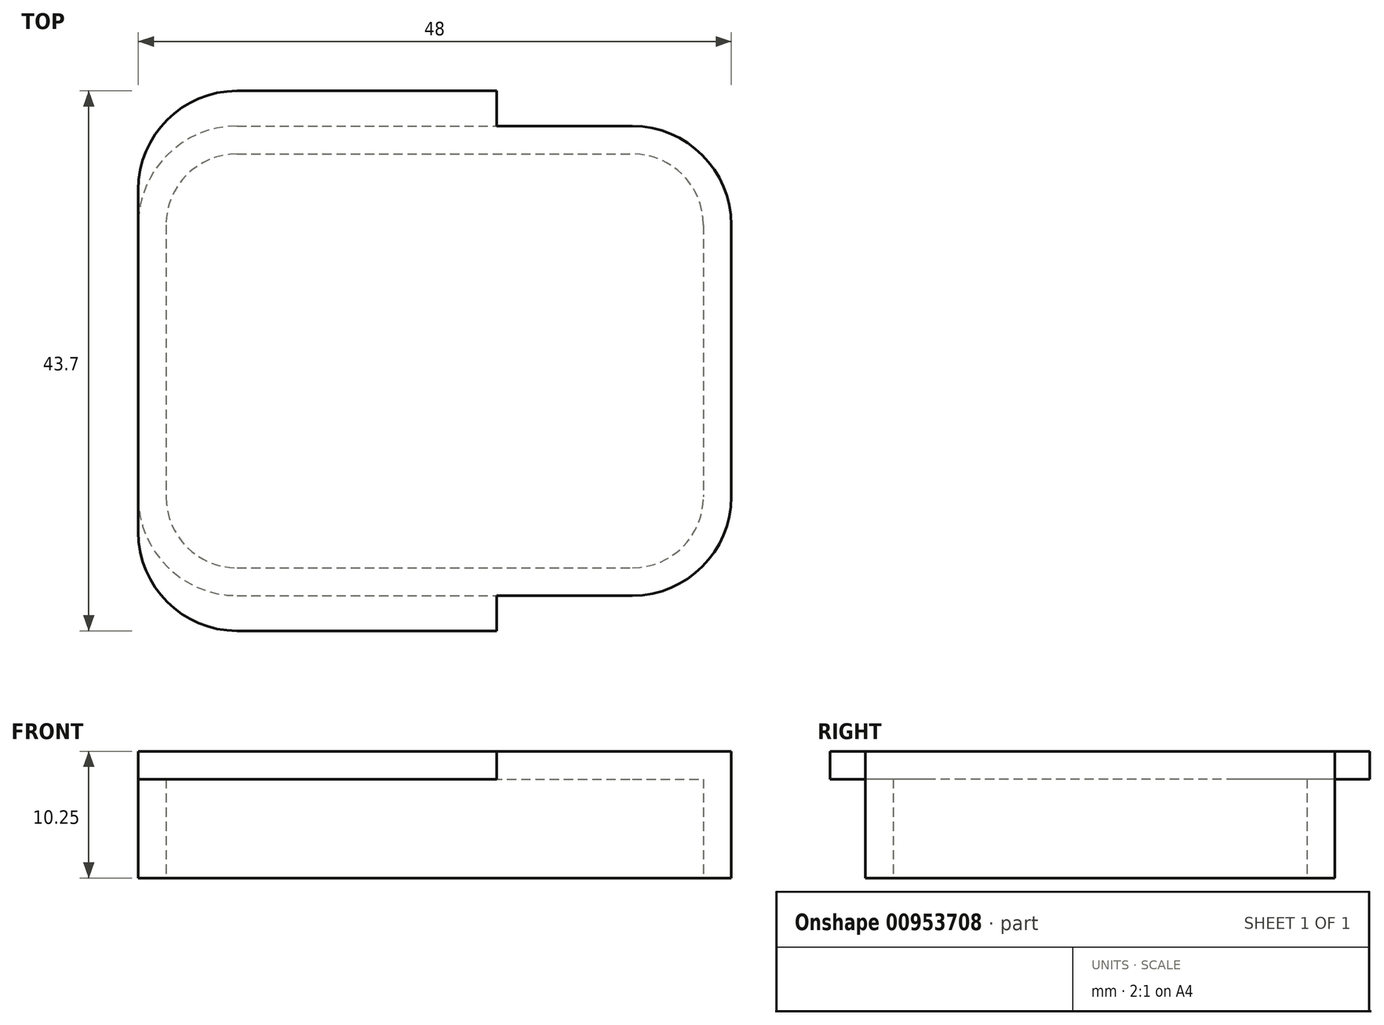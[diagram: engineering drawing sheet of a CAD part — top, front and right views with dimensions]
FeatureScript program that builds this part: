
annotation { "Feature Type Name" : "Feature", "Feature Type Description" : "" }
export const myFeature = defineFeature(function(context is Context, id is Id, definition is map)
    precondition{}
    {
        {
            var Q0;
            Q0=qCreatedBy(makeId("Top.planeOp"),FACE);
            var sketch = newSketch(context, id + "F0", { "sketchPlane" : qUnion([Q0])});
            skLineSegment(sketch, "E0.bottom", {"start": v(-16, 19) * mm, "end": v(16, 19) * mm});
            skLineSegment(sketch, "E0.top", {"start": v(-16, -19) * mm, "end": v(16, -19) * mm});
            skLineSegment(sketch, "E0.left", {"start": v(-24, 11) * mm, "end": v(-24, -11) * mm});
            skLineSegment(sketch, "E0.right", {"start": v(24, 11) * mm, "end": v(24, -11) * mm});
            skPoint(sketch, "E1.visualSharp", {"position": v(24, 19) * mm});
            skArc(sketch, "E1.filletArc", {"start": v(24, 11) * mm, "mid": v(21.66, 16.66) * mm, "end": v(16, 19) * mm});
            skPoint(sketch, "E2.visualSharp", {"position": v(24, -19) * mm});
            skArc(sketch, "E2.filletArc", {"start": v(16, -19) * mm, "mid": v(21.66, -16.66) * mm, "end": v(24, -11) * mm});
            skPoint(sketch, "E3.visualSharp", {"position": v(-24, -19) * mm});
            skArc(sketch, "E3.filletArc", {"start": v(-24, -11) * mm, "mid": v(-21.66, -16.66) * mm, "end": v(-16, -19) * mm});
            skPoint(sketch, "E4.visualSharp", {"position": v(-24, 19) * mm});
            skArc(sketch, "E4.filletArc", {"start": v(-16, 19) * mm, "mid": v(-21.66, 16.66) * mm, "end": v(-24, 11) * mm});
            skSolve(sketch);
        }
        {
            var Q0;
            Q0=makeQuery(id+"F0.imprint","IMPRINT",FACE,{"disambiguationData":[TD([[makeQuery(id+"F0.imprint","IMPRINT",EDGE,{"derivedFrom":sQuery(id+"F0.wireOp",EDGE,"E0.bottom")}),-1.0]])]});
            extrude(context, id + "F1", {"entities" : qUnion([Q0]), "depth" : 10.25 * mm, "offsetDistance" : 25 * mm});
        }
        {
            var Q0;
            Q0=makeQuery(id+"F1.opExtrude","CAP_FACE",FACE,{"disambiguationData":[OSD([sQuery(id+"F0.wireOp",EDGE,"E0.bottom"),sQuery(id+"F0.wireOp",EDGE,"E0.top"),sQuery(id+"F0.wireOp",EDGE,"E0.left"),sQuery(id+"F0.wireOp",EDGE,"E0.right"),sQuery(id+"F0.wireOp",EDGE,"E1.filletArc"),sQuery(id+"F0.wireOp",EDGE,"E2.filletArc"),sQuery(id+"F0.wireOp",EDGE,"E3.filletArc"),sQuery(id+"F0.wireOp",EDGE,"E4.filletArc")])],"isStart":false});
            var sketch = newSketch(context, id + "F2", { "sketchPlane" : qUnion([Q0])});
            skLineSegment(sketch, "E5.bottom", {"start": v(-16, 21.85) * mm, "end": v(5, 21.85) * mm});
            skLineSegment(sketch, "E5.top", {"start": v(-16, -21.85) * mm, "end": v(5, -21.85) * mm});
            skLineSegment(sketch, "E5.left", {"start": v(-24, 13.85) * mm, "end": v(-24, -13.85) * mm});
            skLineSegment(sketch, "E5.right", {"start": v(5, 21.85) * mm, "end": v(5, -21.85) * mm});
            skPoint(sketch, "E6.visualSharp", {"position": v(-24, 21.85) * mm});
            skArc(sketch, "E6.filletArc", {"start": v(-16, 21.85) * mm, "mid": v(-21.66, 19.5) * mm, "end": v(-24, 13.85) * mm});
            skPoint(sketch, "E7.visualSharp", {"position": v(-24, -21.85) * mm});
            skArc(sketch, "E7.filletArc", {"start": v(-24, -13.85) * mm, "mid": v(-21.66, -19.5) * mm, "end": v(-16, -21.85) * mm});
            skSolve(sketch);
        }
        {
            var Q0;
            Q0 = qSketchRegion(id + "F2", true);
            extrude(context, id + "F3", {"entities" : qUnion([Q0]), "operationType" : NewBodyOperationType.ADD, "oppositeDirection" : true, "depth" : 2.25 * mm, "offsetDistance" : 25 * mm});
        }
        {
            var Q0;
            Q0=makeQuery(id+"F1.opExtrude","CAP_FACE",FACE,{"disambiguationData":[OSD([sQuery(id+"F0.wireOp",EDGE,"E0.bottom"),sQuery(id+"F0.wireOp",EDGE,"E0.top"),sQuery(id+"F0.wireOp",EDGE,"E0.left"),sQuery(id+"F0.wireOp",EDGE,"E0.right"),sQuery(id+"F0.wireOp",EDGE,"E1.filletArc"),sQuery(id+"F0.wireOp",EDGE,"E2.filletArc"),sQuery(id+"F0.wireOp",EDGE,"E3.filletArc"),sQuery(id+"F0.wireOp",EDGE,"E4.filletArc")])],"isStart":true});
            shell(context, id + "F4", {"entities" : qUnion([Q0]), "thickness" : 2.25 * mm});
        }
    });
